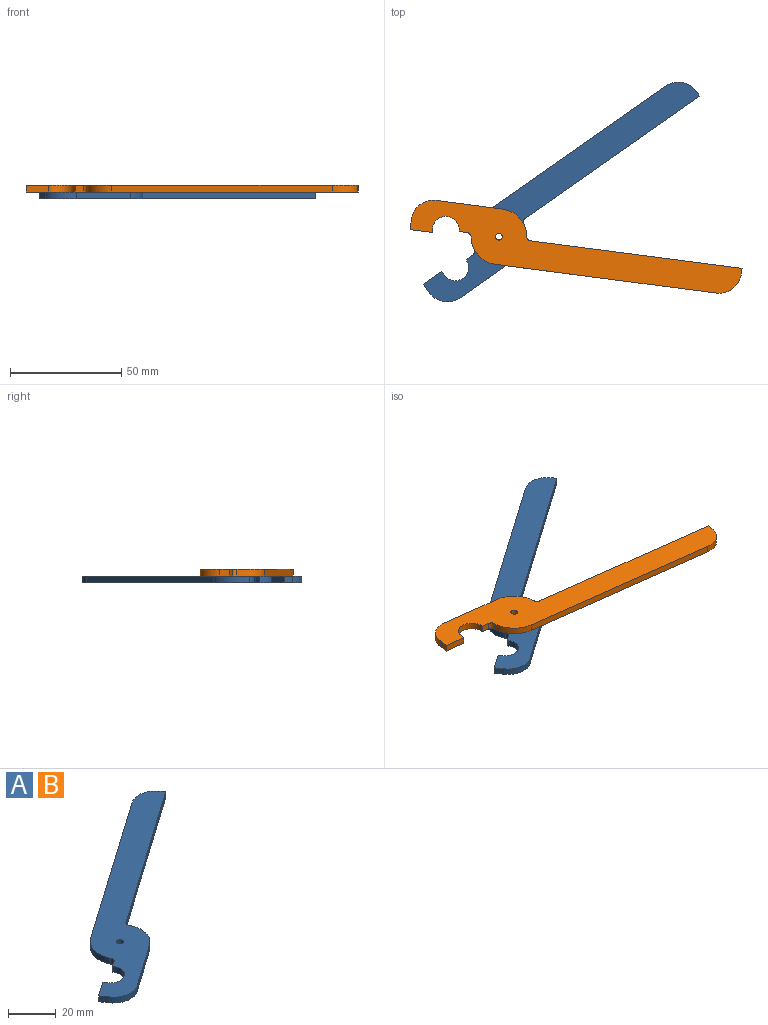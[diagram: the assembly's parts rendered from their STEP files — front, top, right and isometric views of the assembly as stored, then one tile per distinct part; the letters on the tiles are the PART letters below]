
ASSEMBLY  parts=2 mates=1
PART A: 18 faces, bbox 124x98.7x3 mm
  f0: cylinder r=6mm len=10.92mm, axis (0,0,-1), area 56.5mm2, adj f8,f9,f10,f16
  f1: plane 3.69x3mm, normal (-0.82,-0.57,0), area 13.5mm2, adj f9,f10,f11,f17
  f2: plane 24.57x17.21mm, normal (0.57,-0.82,0), area 90mm2, adj f3,f9,f10,f11
  f3: cylinder r=12.5mm len=15.93mm, axis (0,0,-1), area 53.7mm2, adj f2,f9,f10,f13
  f4: plane 78.34x54.86mm, normal (0.57,-0.82,0), area 286.9mm2, adj f5,f9,f10,f13
  f5: plane 3x2.05mm, normal (0.82,0.57,0), area 7.5mm2, adj f4,f9,f10,f12
  f6: plane 81.92x57.36mm, normal (-0.57,0.82,0), area 300mm2, adj f7,f9,f10,f12
  f7: cylinder r=12.5mm len=15.93mm, axis (0,0,-1), area 53.7mm2, adj f6,f9,f10,f14
  f8: plane 3x2.98mm, normal (-0.57,0.82,0), area 10.9mm2, adj f0,f9,f10,f14
  f9: plane 124.02x98.66mm, normal (0,0,1), area 2035.3mm2, adj f0,f1,f2,f3,f4,f5,f6,f7
  f10: plane 124.02x98.66mm, normal (0,0,-1), area 2035.3mm2, adj f0,f1,f2,f3,f4,f5,f6,f7
  f11: cylinder r=10mm len=13.93mm, axis (0,0,-1), area 47.1mm2, adj f1,f2,f9,f10
  f12: cylinder r=10mm len=13.93mm, axis (0,0,-1), area 47.1mm2, adj f5,f6,f9,f10
  f13: cylinder r=2mm len=3mm, axis (0,0,-1), area 8.6mm2, adj f3,f4,f9,f10
  f14: cylinder r=2mm len=3mm, axis (0,0,-1), area 8.6mm2, adj f7,f8,f9,f10
  f15: cylinder r=1.5mm len=3mm, axis (0,0,-1), area 28.3mm2, adj f9,f10
  f16: plane 3x1.64mm, normal (0.82,0.57,0), area 6mm2, adj f0,f9,f10,f17
  f17: plane 8.19x5.74mm, normal (-0.57,0.82,0), area 30mm2, adj f1,f9,f10,f16
PART B: same geometry as A
PLACE A at identity fixed
PLACE B rot(axis=(0.97,0.24,0),180deg) t=(0,0,6)mm
MATE revolute B.f7 <-> A.f7  axis (0,0,-1) through (0,0,3)mm
